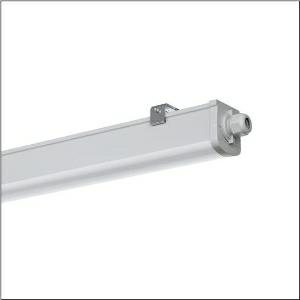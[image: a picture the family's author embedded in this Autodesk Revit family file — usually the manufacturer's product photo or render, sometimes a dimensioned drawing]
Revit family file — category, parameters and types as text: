
# Revit family: monsun_r__31_51fa20dk450b_5819
name_source: partatom
category: Lighting Fixtures
units: mm (PartAtom-declared; Revit-internal decimal feet)

## family parameters
Cut with Voids When Loaded = No
Host = Face
Light Source = No
Part Type = Normal
Room Calculation Point = No
Round Connector Dimension = Use Diameter
Shared = No

## types (1)
- Monsun® 31 (1 x LED, 5100 lm, 38 W, 4000K)
    Apparent Load = 38 VA
    CIE Flux Codes = 42 72 91 92 100
    Color Rendering = 80
    Color Temperature = 4000K
    Default Elevation = 1800 mm
    Description = Monsun® 31, damp-proof luminaire, primary optical cover: diffuser, of PC, frosted, light emission: direct distribution, primary light characteristic: symmetric, installation type: surface-mounted, LED, rated luminous flux: 5.100lm, luminous efficacy: 134lm/W, light colour: 840, colour temperature: 4000K, control gear: ECG, with terminal, 5+1-pole, max. 2.5mm², through-wiring: 3x 2.5mm² + 3x 1.5mm², mains connection: 220..240V, AC, 50/60Hz, rated input power: 38W, housing, luminaire housing, of PC, light grey (RAL 7035), length: 1.158mm, width: 68mm, height: 76mm, protection rating (complete): IP66, insulation class (complete): insulation class II (safety insulation), certification: CE, ENEC, UKCA, protection symbol: D, impact resistance: IK08, permissible operating ambient temperature: -20..+40°C, corresponds to IFS (International Featured Standards) requirements for safety and quality in the food industry, packaging unit: 1 piece
    Height = 77 mm
    Lamp = 1 x LED
    Lamp Light Flux = 5100 lm
    Lamp Power = 38 W
    Lamp count = 1
    Length = 1218 mm
    Luminous efficacy = 134 lm/W
    Manufacturer = Siteco
    ModVariant = No
    Model = 51FA20DK450B
    Mounting Place = Ceiling
    Mounting Type = Surface mounted
    Number of Poles = 1
    OnlyDefault = Yes
    Power Factor = 1
    Product Name = Monsun® 31
    Product group = damp-proof luminaire | ceiling mounted
    ProductGroupID = 300
    Protection Class = Protection class II
    Protection Degree = IP 66
    RLX_Detail_Level = 1
    RlxData = <blob elided: 32717 chars, md5=1a0250ed>
    Socket = socket
    Standby Power = 0 W
    System Light Flux = 5100 lm
    System Power = 38 W
    Type Comments = Product without accessories
    Type Image = l_1006174.jpg
    URL = http://relux.com
    VarID = ---
    Voltage = 0 V
    Weight = 0.00 kg
    Width = 69 mm

## geometry (parser evidence)
native form markers: Blend x4, Sweep x14
no freeform markers — native parametric forms only
